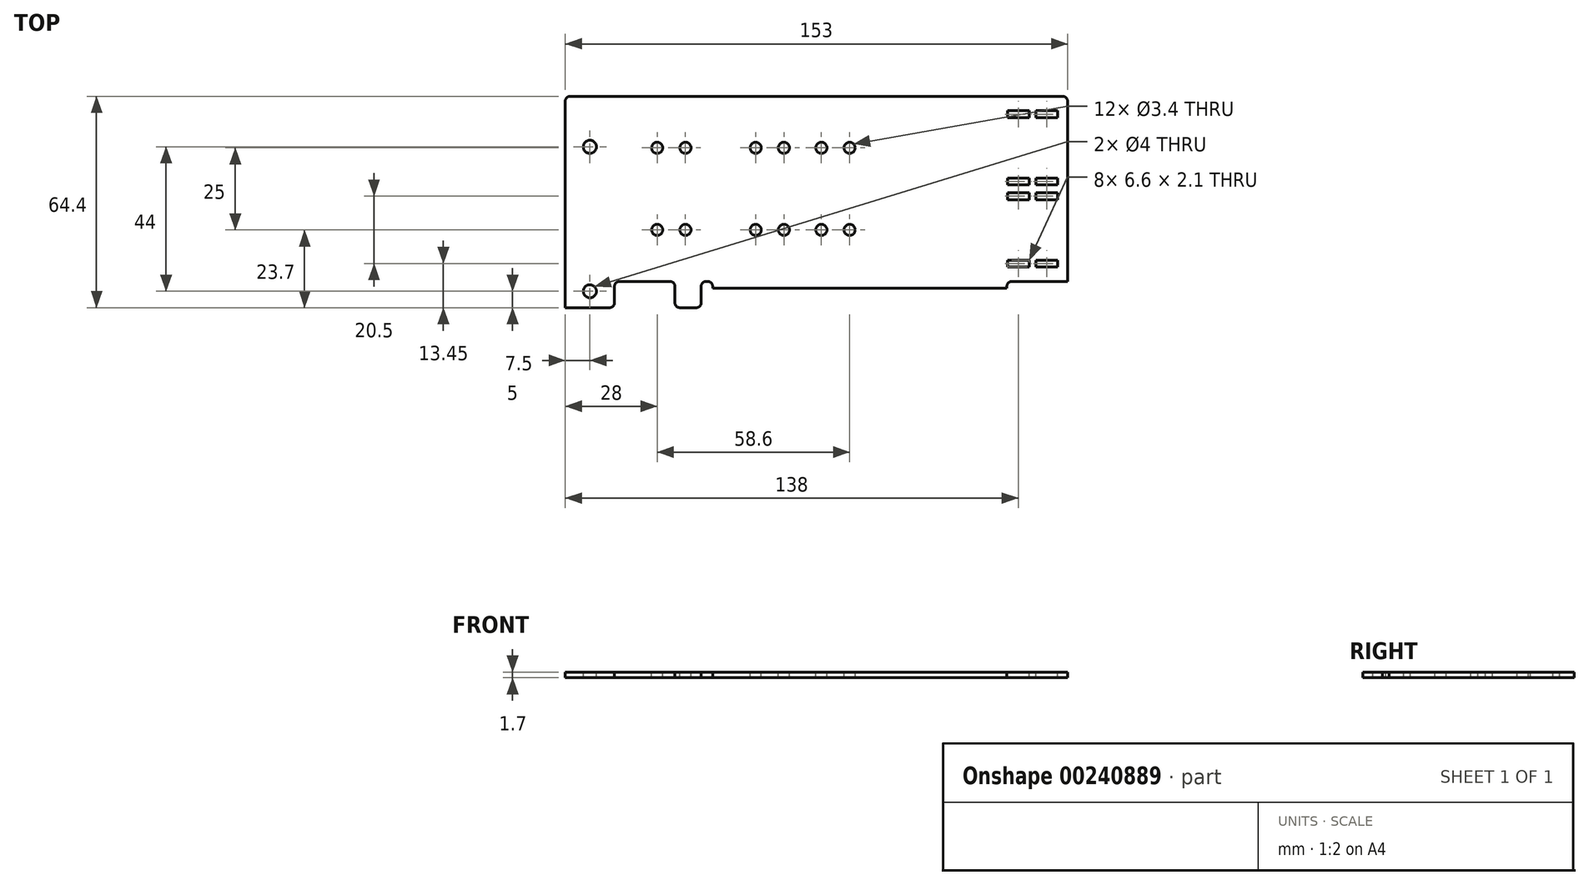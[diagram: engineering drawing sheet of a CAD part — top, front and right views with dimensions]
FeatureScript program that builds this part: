
annotation { "Feature Type Name" : "Feature", "Feature Type Description" : "" }
export const myFeature = defineFeature(function(context is Context, id is Id, definition is map)
    precondition{}
    {
        {
            var Q0;
            Q0=qCreatedBy(makeId("Top.planeOp"),FACE);
            var sketch = newSketch(context, id + "F0", { "sketchPlane" : qUnion([Q0])});
            skLineSegment(sketch, "E0.bottom", {"start": v(76.5, -34.5) * mm, "end": v(-76.5, -34.5) * mm});
            skLineSegment(sketch, "E0.top", {"start": v(76.5, 34.5) * mm, "end": v(-76.5, 34.5) * mm});
            skLineSegment(sketch, "E0.left", {"start": v(76.5, -34.5) * mm, "end": v(76.5, 34.5) * mm});
            skLineSegment(sketch, "E0.right", {"start": v(-76.5, -34.5) * mm, "end": v(-76.5, 34.5) * mm});
            skPoint(sketch, "E0.middle", {"position": v(0, 0) * mm});
            skSolve(sketch);
        }
        {
            var Q0;
            Q0 = qSketchRegion(id + "F0", true);
            extrude(context, id + "F1", {"entities" : qUnion([Q0]), "depth" : 1.7 * mm});
        }
        {
            var Q0;
            Q0=makeQuery(id+"F1.opExtrude","CAP_FACE",FACE,{"disambiguationData":[OSD([sQuery(id+"F0.wireOp",EDGE,"E0.bottom"),sQuery(id+"F0.wireOp",EDGE,"E0.top"),sQuery(id+"F0.wireOp",EDGE,"E0.left"),sQuery(id+"F0.wireOp",EDGE,"E0.right")])],"isStart":false});
            var sketch = newSketch(context, id + "F2", { "sketchPlane" : qUnion([Q0])});
            skLineSegment(sketch, "E1.bottom", {"start": v(-76.5, -34.5) * mm, "end": v(-61.5, -34.5) * mm});
            skLineSegment(sketch, "E1.top", {"start": v(-76.5, -29.9) * mm, "end": v(-61.5, -29.9) * mm});
            skLineSegment(sketch, "E1.left", {"start": v(-76.5, -34.5) * mm, "end": v(-76.5, -29.9) * mm});
            skLineSegment(sketch, "E1.right", {"start": v(-61.5, -34.5) * mm, "end": v(-61.5, -29.9) * mm});
            skLineSegment(sketch, "E2.bottom", {"start": v(-61.5, -34.5) * mm, "end": v(-43.1, -34.5) * mm});
            skLineSegment(sketch, "E2.top", {"start": v(-61.5, -21.9) * mm, "end": v(-43.1, -21.9) * mm});
            skLineSegment(sketch, "E2.left", {"start": v(-61.5, -34.5) * mm, "end": v(-61.5, -21.9) * mm});
            skLineSegment(sketch, "E2.right", {"start": v(-43.1, -34.5) * mm, "end": v(-43.1, -21.9) * mm});
            skLineSegment(sketch, "E3.bottom", {"start": v(-43.1, -29.9) * mm, "end": v(-35.1, -29.9) * mm});
            skLineSegment(sketch, "E3.top", {"start": v(-43.1, -34.5) * mm, "end": v(-35.1, -34.5) * mm});
            skLineSegment(sketch, "E3.left", {"start": v(-43.1, -29.9) * mm, "end": v(-43.1, -34.5) * mm});
            skLineSegment(sketch, "E3.right", {"start": v(-35.1, -29.9) * mm, "end": v(-35.1, -34.5) * mm});
            skLineSegment(sketch, "E4.bottom", {"start": v(-35.1, -34.5) * mm, "end": v(-31.6, -34.5) * mm});
            skLineSegment(sketch, "E4.top", {"start": v(-35.1, -21.9) * mm, "end": v(-31.6, -21.9) * mm});
            skLineSegment(sketch, "E4.left", {"start": v(-35.1, -34.5) * mm, "end": v(-35.1, -21.9) * mm});
            skLineSegment(sketch, "E4.right", {"start": v(-31.6, -34.5) * mm, "end": v(-31.6, -21.9) * mm});
            skLineSegment(sketch, "E5", {"start": v(-31.6, -34.5) * mm, "end": v(-20.3, -34.5) * mm, "construction": true});
            skLineSegment(sketch, "E6.bottom", {"start": v(-20.3, -34.5) * mm, "end": v(-18.4, -34.5) * mm});
            skLineSegment(sketch, "E6.top", {"start": v(-20.3, -26) * mm, "end": v(-18.4, -26) * mm});
            skLineSegment(sketch, "E6.left", {"start": v(-20.3, -34.5) * mm, "end": v(-20.3, -26) * mm});
            skLineSegment(sketch, "E6.right", {"start": v(-18.4, -34.5) * mm, "end": v(-18.4, -26) * mm});
            skLineSegment(sketch, "E7", {"start": v(-18.4, -34.5) * mm, "end": v(58, -34.5) * mm, "construction": true});
            skLineSegment(sketch, "E8.bottom", {"start": v(58, -34.5) * mm, "end": v(76.5, -34.5) * mm});
            skLineSegment(sketch, "E8.top", {"start": v(58, -21.9) * mm, "end": v(76.5, -21.9) * mm});
            skLineSegment(sketch, "E8.left", {"start": v(58, -34.5) * mm, "end": v(58, -21.9) * mm});
            skLineSegment(sketch, "E8.right", {"start": v(76.5, -34.5) * mm, "end": v(76.5, -21.9) * mm});
            skLineSegment(sketch, "E9", {"start": v(-69, -29.9) * mm, "end": v(-69, -24.9) * mm, "construction": true});
            skLineSegment(sketch, "E10", {"start": v(-69, -24.9) * mm, "end": v(-76.5, -24.9) * mm, "construction": true});
            skCircle(sketch, "E11", {"center": v(-69, -24.9) * mm, "radius": 2 * mm});
            skLineSegment(sketch, "E12", {"start": v(-69, -24.9) * mm, "end": v(-69, 19.1) * mm, "construction": true});
            skCircle(sketch, "E13", {"center": v(-69, 19.1) * mm, "radius": 2 * mm});
            skLineSegment(sketch, "E14", {"start": v(76.5, 6.3) * mm, "end": v(71.5, 6.3) * mm, "construction": true});
            skLineSegment(sketch, "E15", {"start": v(76.5, 6.3) * mm, "end": v(76.5, -21.9) * mm, "construction": true});
            skLineSegment(sketch, "E16.MirrorCS", {"start": v(64.8, 30.1) * mm, "end": v(58.2, 30.1) * mm});
            skLineSegment(sketch, "E17.MirrorCS", {"start": v(64.8, 30.1) * mm, "end": v(64.8, 28) * mm});
            skLineSegment(sketch, "E18.MirrorCS", {"start": v(58.2, 30.1) * mm, "end": v(58.2, 28) * mm});
            skLineSegment(sketch, "E19.MirrorCS", {"start": v(64.8, 28) * mm, "end": v(58.2, 28) * mm});
            skLineSegment(sketch, "E20.MirrorCS", {"start": v(64.8, 9.6) * mm, "end": v(58.2, 9.6) * mm});
            skLineSegment(sketch, "E21.MirrorCS", {"start": v(64.8, 7.5) * mm, "end": v(64.8, 9.6) * mm});
            skLineSegment(sketch, "E22.MirrorCS", {"start": v(58.2, 7.5) * mm, "end": v(58.2, 9.6) * mm});
            skLineSegment(sketch, "E23.MirrorCS", {"start": v(64.8, 7.5) * mm, "end": v(58.2, 7.5) * mm});
            skLineSegment(sketch, "E24", {"start": v(61.5, 30.1) * mm, "end": v(61.5, 7.5) * mm, "construction": true});
            skLineSegment(sketch, "E25", {"start": v(61.5, 18.8) * mm, "end": v(76.5, 18.8) * mm, "construction": true});
            skLineSegment(sketch, "E26", {"start": v(76.5, 18.8) * mm, "end": v(76.5, 6.3) * mm, "construction": true});
            skCircle(sketch, "E27", {"center": v(-48.5, 18.8) * mm, "radius": 1.7 * mm});
            skCircle(sketch, "E28", {"center": v(-18.5, 18.8) * mm, "radius": 1.7 * mm});
            skCircle(sketch, "E29", {"center": v(1.5, 18.8) * mm, "radius": 1.7 * mm});
            skCircle(sketch, "E30.1.0.0", {"center": v(-39.9, 18.8) * mm, "radius": 1.7 * mm});
            skCircle(sketch, "E30.1.0.1", {"center": v(-9.9, 18.8) * mm, "radius": 1.7 * mm});
            skCircle(sketch, "E30.1.0.2", {"center": v(10.1, 18.8) * mm, "radius": 1.7 * mm});
            skLineSegment(sketch, "E30.1.0.3", {"start": v(73.4, 7.5) * mm, "end": v(66.8, 7.5) * mm});
            skLineSegment(sketch, "E30.1.0.4", {"start": v(66.8, 7.5) * mm, "end": v(66.8, 9.6) * mm});
            skLineSegment(sketch, "E30.1.0.5", {"start": v(73.4, 7.5) * mm, "end": v(73.4, 9.6) * mm});
            skLineSegment(sketch, "E30.1.0.6", {"start": v(73.4, 9.6) * mm, "end": v(66.8, 9.6) * mm});
            skLineSegment(sketch, "E30.1.0.7", {"start": v(73.4, 28) * mm, "end": v(66.8, 28) * mm});
            skLineSegment(sketch, "E30.1.0.8", {"start": v(73.4, 30.1) * mm, "end": v(73.4, 28) * mm});
            skLineSegment(sketch, "E30.1.0.9", {"start": v(73.4, 30.1) * mm, "end": v(66.8, 30.1) * mm});
            skLineSegment(sketch, "E30.1.0.10", {"start": v(66.8, 30.1) * mm, "end": v(66.8, 28) * mm});
            skLineSegment(sketch, "E30.direction1", {"start": v(-48.5, 18.8) * mm, "end": v(-39.9, 18.8) * mm, "construction": true});
            skLineSegment(sketch, "E31", {"start": v(61.5, 18.8) * mm, "end": v(-48.5, 18.8) * mm, "construction": true});
            skLineSegment(sketch, "E32", {"start": v(61.5, 18.8) * mm, "end": v(-18.5, 18.8) * mm, "construction": true});
            skLineSegment(sketch, "E33", {"start": v(61.5, 18.8) * mm, "end": v(1.5, 18.8) * mm, "construction": true});
            skLineSegment(sketch, "E34.MirrorCS", {"start": v(73.4, -17.5) * mm, "end": v(73.4, -15.4) * mm});
            skLineSegment(sketch, "E35.MirrorCS", {"start": v(58.2, 5.1) * mm, "end": v(58.2, 3) * mm});
            skLineSegment(sketch, "E36.MirrorCS", {"start": v(73.4, 5.1) * mm, "end": v(73.4, 3) * mm});
            skLineSegment(sketch, "E37.MirrorCS", {"start": v(66.8, 5.1) * mm, "end": v(66.8, 3) * mm});
            skLineSegment(sketch, "E38.MirrorCS", {"start": v(58.2, -17.5) * mm, "end": v(58.2, -15.4) * mm});
            skLineSegment(sketch, "E39.MirrorCS", {"start": v(66.8, -17.5) * mm, "end": v(66.8, -15.4) * mm});
            skLineSegment(sketch, "E40.MirrorCS", {"start": v(64.8, -17.5) * mm, "end": v(64.8, -15.4) * mm});
            skLineSegment(sketch, "E41.MirrorCS", {"start": v(64.8, 5.1) * mm, "end": v(64.8, 3) * mm});
            skLineSegment(sketch, "E42.MirrorCS", {"start": v(64.8, 5.1) * mm, "end": v(58.2, 5.1) * mm});
            skLineSegment(sketch, "E43.MirrorCS", {"start": v(61.5, -6.2) * mm, "end": v(1.5, -6.2) * mm, "construction": true});
            skLineSegment(sketch, "E44.MirrorCS", {"start": v(64.8, -17.5) * mm, "end": v(58.2, -17.5) * mm});
            skCircle(sketch, "E45.MirrorC", {"center": v(1.5, -6.2) * mm, "radius": 1.7 * mm});
            skLineSegment(sketch, "E46.MirrorCS", {"start": v(73.4, -17.5) * mm, "end": v(66.8, -17.5) * mm});
            skLineSegment(sketch, "E47.MirrorCS", {"start": v(61.5, -6.2) * mm, "end": v(-18.5, -6.2) * mm, "construction": true});
            skCircle(sketch, "E48.MirrorC", {"center": v(-18.5, -6.2) * mm, "radius": 1.7 * mm});
            skLineSegment(sketch, "E49.MirrorCS", {"start": v(73.4, 3) * mm, "end": v(66.8, 3) * mm});
            skCircle(sketch, "E50.MirrorC", {"center": v(-9.9, -6.2) * mm, "radius": 1.7 * mm});
            skLineSegment(sketch, "E51.MirrorCS", {"start": v(-48.5, -6.2) * mm, "end": v(-39.9, -6.2) * mm, "construction": true});
            skLineSegment(sketch, "E52.MirrorCS", {"start": v(61.5, -6.2) * mm, "end": v(-48.5, -6.2) * mm, "construction": true});
            skLineSegment(sketch, "E53.MirrorCS", {"start": v(61.5, -17.5) * mm, "end": v(61.5, 5.1) * mm, "construction": true});
            skCircle(sketch, "E54.MirrorC", {"center": v(10.1, -6.2) * mm, "radius": 1.7 * mm});
            skLineSegment(sketch, "E55.MirrorCS", {"start": v(61.5, -6.2) * mm, "end": v(76.5, -6.2) * mm, "construction": true});
            skLineSegment(sketch, "E56.MirrorCS", {"start": v(64.8, -15.4) * mm, "end": v(58.2, -15.4) * mm});
            skLineSegment(sketch, "E57.MirrorCS", {"start": v(64.8, 3) * mm, "end": v(58.2, 3) * mm});
            skLineSegment(sketch, "E58.MirrorCS", {"start": v(73.4, 5.1) * mm, "end": v(66.8, 5.1) * mm});
            skLineSegment(sketch, "E59.MirrorCS", {"start": v(73.4, -15.4) * mm, "end": v(66.8, -15.4) * mm});
            skCircle(sketch, "E60.MirrorC", {"center": v(-39.9, -6.2) * mm, "radius": 1.7 * mm});
            skCircle(sketch, "E61.MirrorC", {"center": v(-48.5, -6.2) * mm, "radius": 1.7 * mm});
            skSolve(sketch);
        }
        {
            var Q0;
            Q0 = qSketchRegion(id + "F2", true);
            extrude(context, id + "F3", {"entities" : qUnion([Q0]), "operationType" : NewBodyOperationType.REMOVE, "endBound" : BoundingType.THROUGH_ALL, "oppositeDirection" : true, "depth" : 25 * mm});
        }
        {
            var Q0;
            Q0=qCreatedBy(makeId("Top.planeOp"),FACE);
            var sketch = newSketch(context, id + "F4", { "sketchPlane" : qUnion([Q0])});
            skLineSegment(sketch, "E62.bottom", {"start": v(-31.6, -23.95) * mm, "end": v(58, -23.95) * mm});
            skLineSegment(sketch, "E62.top", {"start": v(-31.6, -34.5) * mm, "end": v(58, -34.5) * mm});
            skLineSegment(sketch, "E62.left", {"start": v(-31.6, -23.95) * mm, "end": v(-31.6, -34.5) * mm});
            skLineSegment(sketch, "E62.right", {"start": v(58, -23.95) * mm, "end": v(58, -34.5) * mm});
            skPoint(sketch, "E63.0", {"position": v(-31.6, -21.9) * mm});
            skPoint(sketch, "E64.0", {"position": v(-20.3, -26) * mm});
            skPoint(sketch, "E65.0", {"position": v(-18.4, -26) * mm});
            skPoint(sketch, "E66.0", {"position": v(58, -21.9) * mm});
            skPoint(sketch, "E67.0", {"position": v(-31.6, -34.5) * mm});
            skPoint(sketch, "E68.0", {"position": v(58, -34.5) * mm});
            skLineSegment(sketch, "E69", {"start": v(-31.6, -21.9) * mm, "end": v(-31.6, -26) * mm, "construction": true});
            skSolve(sketch);
        }
        {
            var Q0;
            Q0 = qSketchRegion(id + "F4", true);
            extrude(context, id + "F5", {"entities" : qUnion([Q0]), "operationType" : NewBodyOperationType.REMOVE, "endBound" : BoundingType.THROUGH_ALL, "depth" : 25 * mm});
        }
        {
            var Q0;
            Q0=makeQuery(id+"F3.boolean.opBoolean","COPY",EDGE,{"derivedFrom":makeQuery(id+"F3.opExtrude","SWEPT_EDGE",EDGE,{"disambiguationData":[OSD([sQuery(id+"F2.wireOp",EDGE,"E4.top"),sQuery(id+"F2.wireOp",EDGE,"E4.left")])]})});
            var Q1;
            Q1=makeQuery(id+"F3.boolean.opBoolean","COPY",EDGE,{"derivedFrom":makeQuery(id+"F3.opExtrude","SWEPT_EDGE",EDGE,{"disambiguationData":[OSD([sQuery(id+"F2.wireOp",EDGE,"E4.top"),sQuery(id+"F2.wireOp",EDGE,"E4.right")])]})});
            var Q2;
            Q2=makeQuery(id+"F3.boolean.opBoolean","COPY",EDGE,{"derivedFrom":makeQuery(id+"F3.opExtrude","SWEPT_EDGE",EDGE,{"disambiguationData":[OSD([sQuery(id+"F2.wireOp",EDGE,"E2.top"),sQuery(id+"F2.wireOp",EDGE,"E2.right")])]})});
            var Q3;
            Q3=makeQuery(id+"F3.boolean.opBoolean","COPY",EDGE,{"derivedFrom":makeQuery(id+"F3.opExtrude","SWEPT_EDGE",EDGE,{"disambiguationData":[OSD([sQuery(id+"F2.wireOp",EDGE,"E8.top"),sQuery(id+"F2.wireOp",EDGE,"E8.left")])]})});
            var Q4;
            Q4=makeQuery(id+"F3.boolean.opBoolean","COPY",EDGE,{"derivedFrom":makeQuery(id+"F3.opExtrude","SWEPT_EDGE",EDGE,{"disambiguationData":[OSD([sQuery(id+"F0.wireOp",EDGE,"E0.bottom"),sQuery(id+"F2.wireOp",EDGE,"E8.bottom"),sQuery(id+"F2.wireOp",EDGE,"E8.left")])]})});
            var Q5;
            Q5=makeQuery(id+"F3.boolean.opBoolean","COPY",EDGE,{"derivedFrom":makeQuery(id+"F3.opExtrude","SWEPT_EDGE",EDGE,{"disambiguationData":[OSD([sQuery(id+"F0.wireOp",EDGE,"E0.left"),sQuery(id+"F2.wireOp",EDGE,"E8.top"),sQuery(id+"F2.wireOp",EDGE,"E8.right")])]})});
            var Q6;
            Q6=makeQuery(id+"F3.boolean.opBoolean","COPY",EDGE,{"derivedFrom":makeQuery(id+"F3.opExtrude","SWEPT_EDGE",EDGE,{"disambiguationData":[OSD([sQuery(id+"F0.wireOp",EDGE,"E0.bottom"),sQuery(id+"F2.wireOp",EDGE,"E6.bottom"),sQuery(id+"F2.wireOp",EDGE,"E6.left")])]})});
            var Q7;
            Q7=makeQuery(id+"F3.boolean.opBoolean","COPY",EDGE,{"derivedFrom":makeQuery(id+"F3.opExtrude","SWEPT_EDGE",EDGE,{"disambiguationData":[OSD([sQuery(id+"F0.wireOp",EDGE,"E0.bottom"),sQuery(id+"F2.wireOp",EDGE,"E6.bottom"),sQuery(id+"F2.wireOp",EDGE,"E6.right")])]})});
            var Q8;
            Q8=makeQuery(id+"F3.boolean.opBoolean","COPY",EDGE,{"derivedFrom":makeQuery(id+"F3.opExtrude","SWEPT_EDGE",EDGE,{"disambiguationData":[OSD([sQuery(id+"F0.wireOp",EDGE,"E0.bottom"),sQuery(id+"F2.wireOp",EDGE,"E4.bottom"),sQuery(id+"F2.wireOp",EDGE,"E4.right")])]})});
            var Q9;
            Q9=makeQuery(id+"F3.boolean.opBoolean","COPY",EDGE,{"derivedFrom":makeQuery(id+"F3.opExtrude","SWEPT_EDGE",EDGE,{"disambiguationData":[OSD([sQuery(id+"F2.wireOp",EDGE,"E3.bottom"),sQuery(id+"F2.wireOp",EDGE,"E4.left")])]})});
            var Q10;
            Q10=makeQuery(id+"F3.boolean.opBoolean","COPY",EDGE,{"derivedFrom":makeQuery(id+"F3.opExtrude","SWEPT_EDGE",EDGE,{"disambiguationData":[OSD([sQuery(id+"F2.wireOp",EDGE,"E2.right"),sQuery(id+"F2.wireOp",EDGE,"E3.bottom"),sQuery(id+"F2.wireOp",EDGE,"E3.left")])]})});
            var Q11;
            Q11=makeQuery(id+"F3.boolean.opBoolean","COPY",EDGE,{"derivedFrom":makeQuery(id+"F3.opExtrude","SWEPT_EDGE",EDGE,{"disambiguationData":[OSD([sQuery(id+"F0.wireOp",EDGE,"E0.right"),sQuery(id+"F2.wireOp",EDGE,"E1.top"),sQuery(id+"F2.wireOp",EDGE,"E1.left")])]})});
            var Q12;
            Q12=makeQuery(id+"F3.boolean.opBoolean","COPY",EDGE,{"derivedFrom":makeQuery(id+"F3.opExtrude","SWEPT_EDGE",EDGE,{"disambiguationData":[OSD([sQuery(id+"F2.wireOp",EDGE,"E1.top"),sQuery(id+"F2.wireOp",EDGE,"E2.left")])]})});
            var Q13;
            Q13=makeQuery(id+"F3.boolean.opBoolean","COPY",EDGE,{"derivedFrom":makeQuery(id+"F3.opExtrude","SWEPT_EDGE",EDGE,{"disambiguationData":[OSD([sQuery(id+"F2.wireOp",EDGE,"E2.top"),sQuery(id+"F2.wireOp",EDGE,"E2.left")])]})});
            var Q14;
            Q14=makeQuery(id+"F1.opExtrude","SWEPT_EDGE",EDGE,{"disambiguationData":[OSD([sQuery(id+"F0.wireOp",EDGE,"E0.top"),sQuery(id+"F0.wireOp",EDGE,"E0.left")])]});
            var Q15;
            Q15=makeQuery(id+"F1.opExtrude","SWEPT_EDGE",EDGE,{"disambiguationData":[OSD([sQuery(id+"F0.wireOp",EDGE,"E0.top"),sQuery(id+"F0.wireOp",EDGE,"E0.right")])]});
            fillet(context, id + "F6", {"entities" : qUnion([Q0, Q1, Q2, Q3, Q4, Q5, Q6, Q7, Q8, Q9, Q10, Q11, Q12, Q13, Q14, Q15]), "radius" : 1.5 * mm, "tangentPropagation" : true, "allowEdgeOverflow" : false});
        }
    });
